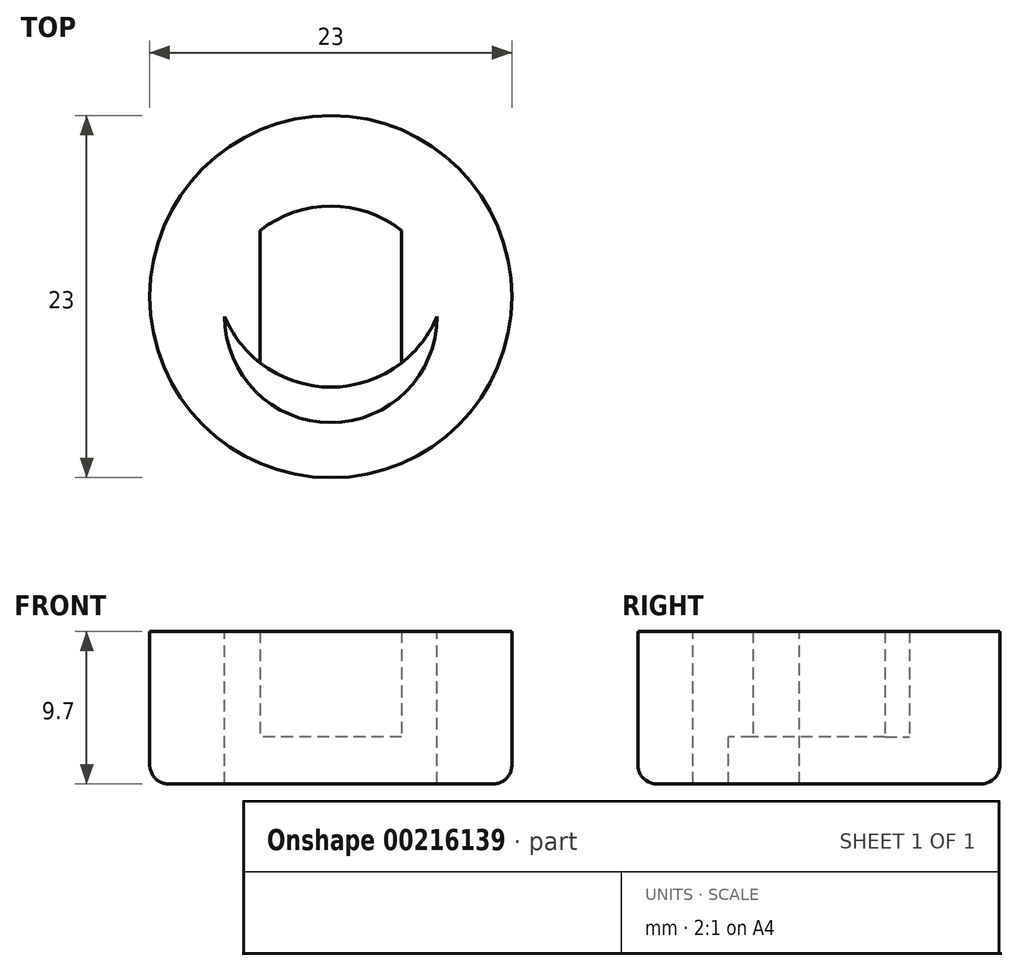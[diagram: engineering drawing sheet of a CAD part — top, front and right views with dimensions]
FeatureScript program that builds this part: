
annotation { "Feature Type Name" : "Feature", "Feature Type Description" : "" }
export const myFeature = defineFeature(function(context is Context, id is Id, definition is map)
    precondition{}
    {
        {
            var Q0;
            Q0=qCreatedBy(makeId("Top.planeOp"),FACE);
            var sketch = newSketch(context, id + "F0", { "sketchPlane" : qUnion([Q0])});
            skCircle(sketch, "E0", {"center": v(0, 0) * mm, "radius": 11.5 * mm});
            skLineSegment(sketch, "E1", {"start": v(0, 16.95) * mm, "end": v(0, -19.62) * mm, "construction": true});
            skLineSegment(sketch, "E2", {"start": v(-26.12, 0) * mm, "end": v(29.85, 0) * mm, "construction": true});
            skArc(sketch, "E3", {"start": v(6.75, 1.25) * mm, "mid": v(0, 8) * mm, "end": v(-6.75, 1.25) * mm});
            skArc(sketch, "E4.MirrorC", {"start": v(6.75, -1.25) * mm, "mid": v(0, -8) * mm, "end": v(-6.75, -1.25) * mm});
            skLineSegment(sketch, "E5", {"start": v(-6.75, 1.25) * mm, "end": v(-6.75, -1.25) * mm});
            skLineSegment(sketch, "E6.MirrorCS", {"start": v(6.75, 1.25) * mm, "end": v(6.75, -1.25) * mm});
            skArc(sketch, "E7", {"start": v(6.75, 1.25) * mm, "mid": v(0, 5.75) * mm, "end": v(-6.75, 1.25) * mm});
            skArc(sketch, "E8", {"start": v(-6.75, -1.25) * mm, "mid": v(0, -5.75) * mm, "end": v(6.75, -1.25) * mm});
            skLineSegment(sketch, "E9", {"start": v(-4.5, 4.2) * mm, "end": v(-4.5, -4.2) * mm});
            skLineSegment(sketch, "E10.MirrorCS", {"start": v(4.5, 4.2) * mm, "end": v(4.5, -4.2) * mm});
            skSolve(sketch);
        }
        {
            var Q0;
            Q0 = qSketchRegion(id + "F0", true);
            var Q1;
            Q1=makeQuery(id+"F0.imprint","IMPRINT",FACE,{"disambiguationData":[TD([[makeQuery(id+"F0.imprint","IMPRINT",EDGE,{"derivedFrom":sQuery(id+"F0.wireOp",EDGE,"E3")}),1.0]])]});
            var Q2;
            {var subQ0=sQuery(id+"F0.wireOp",EDGE,"E5");Q2=makeQuery(id+"F0.imprint","IMPRINT",FACE,{"disambiguationData":[TD([[makeQuery(id+"F0.imprint","IMPRINT",EDGE,{"derivedFrom":subQ0}),1.0]])]});}
            var Q3;
            {var subQ0=sQuery(id+"F0.wireOp",EDGE,"E9");Q3=makeQuery(id+"F0.imprint","IMPRINT",FACE,{"disambiguationData":[TD([[makeQuery(id+"F0.imprint","IMPRINT",EDGE,{"derivedFrom":subQ0}),1.0]])]});}
            var Q4;
            {var subQ0=sQuery(id+"F0.wireOp",EDGE,"E4.MirrorC");Q4=makeQuery(id+"F0.imprint","IMPRINT",FACE,{"disambiguationData":[TD([[makeQuery(id+"F0.imprint","IMPRINT",EDGE,{"derivedFrom":subQ0}),-1.0]])]});}
            var Q5;
            {var subQ0=sQuery(id+"F0.wireOp",EDGE,"E6.MirrorCS");Q5=makeQuery(id+"F0.imprint","IMPRINT",FACE,{"disambiguationData":[TD([[makeQuery(id+"F0.imprint","IMPRINT",EDGE,{"derivedFrom":subQ0}),-1.0]])]});}
            extrude(context, id + "F1", {"entities" : qUnion([Q0, Q1, Q2, Q3, Q4, Q5]), "oppositeDirection" : true, "depth" : 3 * mm});
        }
        {
            var Q0;
            Q0=makeQuery(id+"F1.opExtrude","CAP_EDGE",EDGE,{"disambiguationData":[OSD([sQuery(id+"F0.wireOp",EDGE,"E0")])],"isStart":false});
            fillet(context, id + "F2", {"entities" : qUnion([Q0]), "radius" : 1.2 * mm, "tangentPropagation" : true, "allowEdgeOverflow" : false});
        }
        {
            var Q0;
            {var subQ0=sQuery(id+"F0.wireOp",EDGE,"E5");Q0=makeQuery(id+"F0.imprint","IMPRINT",FACE,{"disambiguationData":[TD([[makeQuery(id+"F0.imprint","IMPRINT",EDGE,{"derivedFrom":subQ0}),1.0]])]});}
            var Q1;
            {var subQ0=sQuery(id+"F0.wireOp",EDGE,"E3");Q1=makeQuery(id+"F0.imprint","IMPRINT",FACE,{"disambiguationData":[TD([[makeQuery(id+"F0.imprint","IMPRINT",EDGE,{"derivedFrom":subQ0}),1.0]])]});}
            var Q2;
            {var subQ0=sQuery(id+"F0.wireOp",EDGE,"E6.MirrorCS");Q2=makeQuery(id+"F0.imprint","IMPRINT",FACE,{"disambiguationData":[TD([[makeQuery(id+"F0.imprint","IMPRINT",EDGE,{"derivedFrom":subQ0}),-1.0]])]});}
            var Q3;
            {var subQ0=sQuery(id+"F0.wireOp",EDGE,"E4.MirrorC");Q3=makeQuery(id+"F0.imprint","IMPRINT",FACE,{"disambiguationData":[TD([[makeQuery(id+"F0.imprint","IMPRINT",EDGE,{"derivedFrom":subQ0}),-1.0]])]});}
            extrude(context, id + "F3", {"entities" : qUnion([Q0, Q1, Q2, Q3]), "operationType" : NewBodyOperationType.ADD, "depth" : 6.7 * mm});
        }
    });
